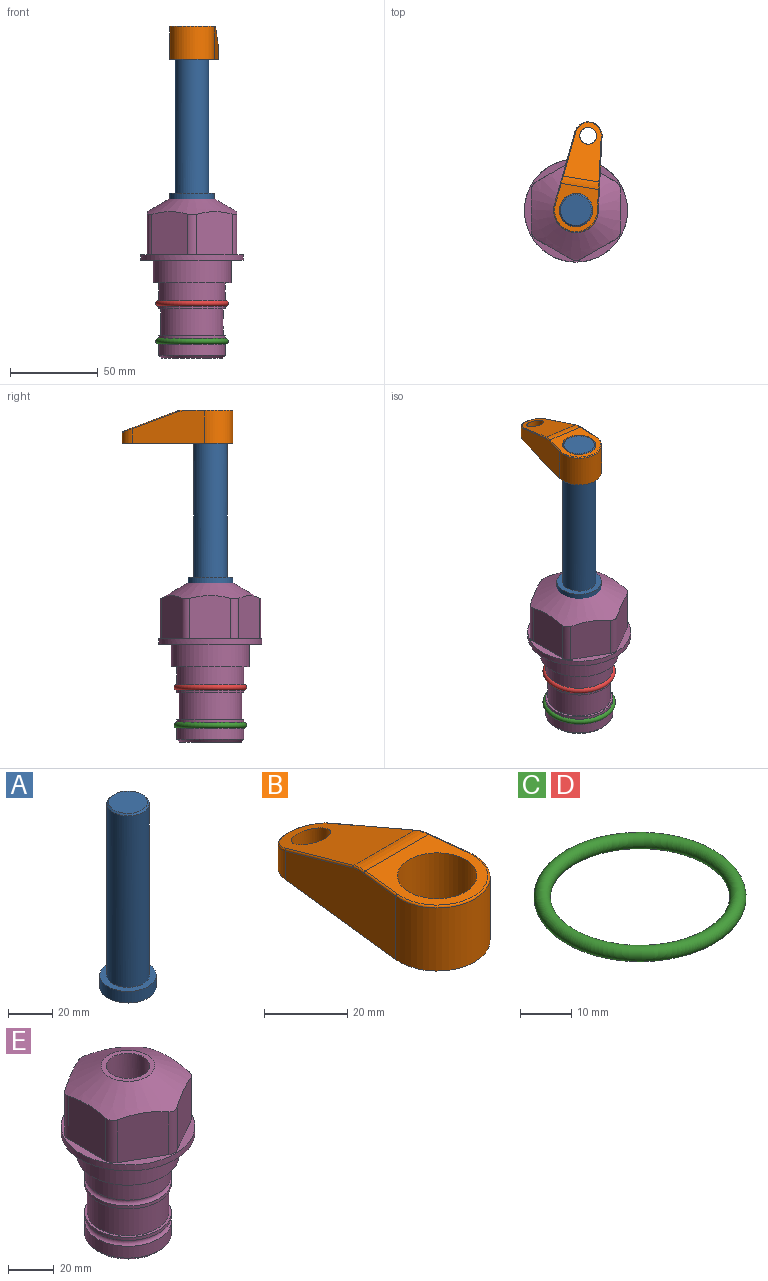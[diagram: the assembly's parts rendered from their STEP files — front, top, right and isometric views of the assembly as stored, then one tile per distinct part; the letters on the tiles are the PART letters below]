
ASSEMBLY  parts=5 mates=3
PART A: 6 faces, bbox 25.4x25.4x101.6 mm
  f0: plane 17.46x17.46mm, normal (0,0,1), area 239.5mm2, adj f5
  f1: plane 25.4x25.4mm, normal (0,0,-1), area 506.7mm2, adj f2
  f2: cylinder r=12.7mm len=25.4mm, axis (0,0,1), area 506.7mm2, adj f1,f3
  f3: plane 25.4x25.4mm, normal (0,0,1), area 221.7mm2, adj f2,f4
  f4: cylinder r=9.53mm len=94.46mm, axis (0,0,1), area 5653mm2, adj f3,f5
  f5: cone r=8.73mm half-angle=45deg, axis (0,0,-1), area 64.4mm2, adj f0,f4
PART B: 44 faces, bbox 27.5x64.5x19.1 mm
  f0: plane 2.3x0.95mm, normal (0,0,-1), area 1mm2, adj f25,f30,f34
  f1: plane 63.5x25.4mm, normal (0,0,-1), area 561.7mm2, adj f2,f3,f4,f5,f6,f7,f19,f20
  f2: cylinder r=12.7mm len=25.4mm, axis (0,0,-1), area 792.2mm2, adj f1,f3,f5,f13
  f3: plane 42.33x18.54mm, normal (0.99,0.11,0), area 647mm2, adj f1,f2,f4,f11,f12,f14
  f4: cylinder r=7.94mm len=15.78mm, axis (0,0,-1), area 158.6mm2, adj f1,f3,f5,f16
  f5: plane 42.33x18.54mm, normal (-0.99,0.11,0), area 647mm2, adj f1,f2,f4,f15,f17,f18
  f6: cylinder r=9.53mm len=19.05mm, axis (0,0,-1), area 1140.1mm2, adj f1,f8
  f7: cylinder r=4.76mm len=10.98mm, axis (0,0,-1), area 276.1mm2, adj f1,f9
  f8: plane 25.83x24.38mm, normal (0,0,1), area 262.2mm2, adj f6,f10,f11,f13,f15
  f9: plane 32.49x20.55mm, normal (0,0.34,0.94), area 489.9mm2, adj f7,f10,f14,f16,f18
  f10: cylinder r=12.7mm len=21.49mm, axis (-1,0,0), area 93.2mm2, adj f8,f9,f12,f17
  f11: cylinder r=0.51mm len=12.34mm, axis (0.11,-0.99,0), area 9.9mm2, adj f3,f8,f12,f13
  f12: bspline ~7.62x1.64mm, area 3.5mm2, adj f3,f10,f11,f14
  f13: torus R=12.19mm, axis (0,0,1), area 33.6mm2, adj f2,f8,f11,f15
  f14: cylinder r=0.51mm len=26.01mm, axis (0.1,-0.93,0.34), area 21.6mm2, adj f3,f9,f12,f16
  f15: cylinder r=0.51mm len=12.34mm, axis (0.11,0.99,0), area 9.9mm2, adj f5,f8,f13,f17
  f16: bspline ~15.78x7.05mm, area 15.7mm2, adj f4,f9,f14,f18
  f17: bspline ~7.62x1.64mm, area 3.5mm2, adj f5,f10,f15,f18
  f18: cylinder r=0.51mm len=26.01mm, axis (0.1,0.93,-0.34), area 21.6mm2, adj f5,f9,f16,f17
  f19: plane 21.6x14.29mm, normal (-0.99,-0.11,0), area 242.6mm2, adj f1,f26,f28,f34,f36,f38
  f20: plane 21.6x14.29mm, normal (0.99,-0.11,0), area 242.6mm2, adj f1,f27,f29,f37,f39,f41
  f21: cylinder r=12.7mm len=14.29mm, axis (0,0,-1), area 173.2mm2, adj f1,f26,f27,f30,f31,f33
  f22: cylinder r=7.94mm len=7.63mm, axis (0,0,-1), area 53.8mm2, adj f1,f28,f29,f42
  f23: plane 2.3x0.95mm, normal (0,0,-1), area 1mm2, adj f25,f33,f37
  f24: plane 17.94x12.32mm, normal (0,-0.34,-0.94), area 191.2mm2, adj f25,f38,f41,f42
  f25: cylinder r=9.53mm len=12.93mm, axis (-1,0,0), area 37.5mm2, adj f0,f23,f24,f31,f36,f39
  f26: cylinder r=1.59mm len=14.29mm, axis (0,0,-1), area 49mm2, adj f1,f19,f21,f32
  f27: cylinder r=1.59mm len=14.29mm, axis (0,0,-1), area 49mm2, adj f1,f20,f21,f35
  f28: cylinder r=1.59mm len=7.28mm, axis (0,0,-1), area 22.1mm2, adj f1,f19,f22,f40
  f29: cylinder r=1.59mm len=7.28mm, axis (0,0,-1), area 22.1mm2, adj f1,f20,f22,f43
  f30: torus R=14.29mm, axis (0,0,1), area 5.8mm2, adj f0,f21,f31,f32
  f31: bspline ~11.06x2.73mm, area 20.8mm2, adj f21,f25,f30,f33
  f32: sphere r=1.59mm, area 5.4mm2, adj f26,f30,f34
  f33: torus R=14.29mm, axis (0,0,1), area 5.8mm2, adj f21,f23,f31,f35
  f34: cylinder r=1.59mm len=1.68mm, axis (-0.11,0.99,0), area 2.4mm2, adj f0,f19,f32,f36
  f35: sphere r=1.59mm, area 5.4mm2, adj f27,f33,f37
  f36: bspline ~5.82x2.33mm, area 7.7mm2, adj f19,f25,f34,f38
  f37: cylinder r=1.59mm len=1.68mm, axis (0.11,0.99,0), area 2.4mm2, adj f20,f23,f35,f39
  f38: cylinder r=1.59mm len=18.33mm, axis (0.1,-0.93,0.34), area 46.7mm2, adj f19,f24,f36,f40
  f39: bspline ~5.82x2.33mm, area 7.7mm2, adj f20,f25,f37,f41
  f40: sphere r=1.59mm, area 3.6mm2, adj f28,f38,f42
  f41: cylinder r=1.59mm len=18.33mm, axis (0.1,0.93,-0.34), area 46.7mm2, adj f20,f24,f39,f43
  f42: bspline ~8.31x1.84mm, area 15.3mm2, adj f22,f24,f40,f43
  f43: sphere r=1.59mm, area 3.6mm2, adj f29,f41,f42
PART C: 1 faces, bbox 44.7x44.7x3.2 mm
  f0: torus R=19.05mm, axis (0,0,1), area 1193.9mm2
PART D: same geometry as C
PART E: 36 faces, bbox 58.7x58.7x91.2 mm
  f0: cylinder r=17.78mm len=35.56mm, axis (0,0,1), area 1670.8mm2, adj f23,f24,f31
  f1: cylinder r=19.05mm len=38.1mm, axis (0,0,1), area 1191.9mm2, adj f26,f27,f30
  f2: plane 58.66x58.66mm, normal (0,0,-1), area 1150.6mm2, adj f3,f28
  f3: cylinder r=29.33mm len=58.66mm, axis (0,0,-1), area 585.1mm2, adj f2,f4
  f4: plane 58.66x58.66mm, normal (0,0,1), area 475.9mm2, adj f3,f5,f6,f7,f8,f9,f10,f11
  f5: plane 24.5x20.32mm, normal (-0.5,0.87,0), area 562.8mm2, adj f4,f15,f16,f17
  f6: plane 24.5x20.32mm, normal (0.5,0.87,0), area 562.8mm2, adj f4,f14,f15,f17
  f7: plane 24.5x23.48mm, normal (1,0,0), area 562.8mm2, adj f4,f13,f14,f17
  f8: plane 24.5x20.32mm, normal (0.5,-0.87,0), area 562.8mm2, adj f4,f12,f13,f17
  f9: plane 24.5x20.32mm, normal (-0.5,-0.87,0), area 562.8mm2, adj f4,f11,f12,f17
  f10: plane 24.5x23.48mm, normal (-1,0,0), area 562.8mm2, adj f4,f11,f16,f17
  f11: cylinder r=5.08mm len=23.01mm, axis (0,0,-1), area 121.2mm2, adj f4,f9,f10,f17
  f12: cylinder r=5.08mm len=23.01mm, axis (0,0,-1), area 121.2mm2, adj f4,f8,f9,f17
  f13: cylinder r=5.08mm len=23.01mm, axis (0,0,-1), area 121.2mm2, adj f4,f7,f8,f17
  f14: cylinder r=5.08mm len=23.01mm, axis (0,0,-1), area 121.2mm2, adj f4,f6,f7,f17
  f15: cylinder r=5.08mm len=23.01mm, axis (0,0,-1), area 121.2mm2, adj f4,f5,f6,f17
  f16: cylinder r=5.08mm len=23.01mm, axis (0,0,-1), area 121.2mm2, adj f4,f5,f10,f17
  f17: cone r=11.73mm half-angle=60deg, axis (0,0,-1), area 2071.8mm2, adj f5,f6,f7,f8,f9,f10,f11,f12
  f18: plane 23.46x23.46mm, normal (0,0,1), area 147.4mm2, adj f17,f35
  f19: plane 34.93x34.93mm, normal (0,0,-1), area 958mm2, adj f29
  f20: cylinder r=19.05mm len=38.1mm, axis (0,0,1), area 760.1mm2, adj f21,f29
  f21: torus R=19.05mm, axis (0,0,1), area 565.3mm2, adj f20,f22
  f22: cylinder r=19.05mm len=38.1mm, axis (0,0,1), area 190mm2, adj f21,f23
  f23: plane 38.1x38.1mm, normal (0,0,1), area 146.9mm2, adj f0,f22
  f24: plane 38.1x38.1mm, normal (0,0,-1), area 146.9mm2, adj f0,f25
  f25: cylinder r=19.05mm len=38.1mm, axis (0,0,1), area 190mm2, adj f24,f26
  f26: torus R=19.05mm, axis (0,0,1), area 565.3mm2, adj f1,f25
  f27: plane 44.45x44.45mm, normal (0,0,-1), area 411.7mm2, adj f1,f28
  f28: cylinder r=22.23mm len=44.45mm, axis (0,0,1), area 1773.5mm2, adj f2,f27
  f29: cone r=19.05mm half-angle=45deg, axis (0,0,1), area 257.5mm2, adj f19,f20
  f30: cylinder r=3.17mm len=6.75mm, axis (-1,0,0), area 128mm2, adj f1,f33
  f31: cylinder r=3.17mm len=6.35mm, axis (-1,0,0), area 102.5mm2, adj f0,f33
  f32: plane 25.4x25.4mm, normal (0,0,1), area 506.7mm2, adj f33
  f33: cylinder r=12.7mm len=66.42mm, axis (0,0,-1), area 5236.2mm2, adj f30,f31,f32,f34
  f34: cone r=9.53mm half-angle=30deg, axis (0,0,-1), area 443.4mm2, adj f33,f35
  f35: cylinder r=9.53mm len=19.05mm, axis (0,0,-1), area 849mm2, adj f18,f34
PLACE A rot(axis=(0,0,1),80.7deg) t=(0,0,59.66)mm
PLACE B rot(axis=(0,0,-1),9.3deg) t=(0,0,114.27)mm
PLACE C t=(0,0,-21.59)mm
PLACE D at identity
PLACE E at identity fixed
MATE fastened C.f0 <-> E.f0  axis (0,0,1) through (0,0,-46.1)mm
MATE cylindrical A.f2 <-> E.f0  axis (0,0,1) through (0,0,85.3)mm
MATE fastened B.f2 <-> A.f2  axis (0,0,1) through (0,0,133.32)mm
